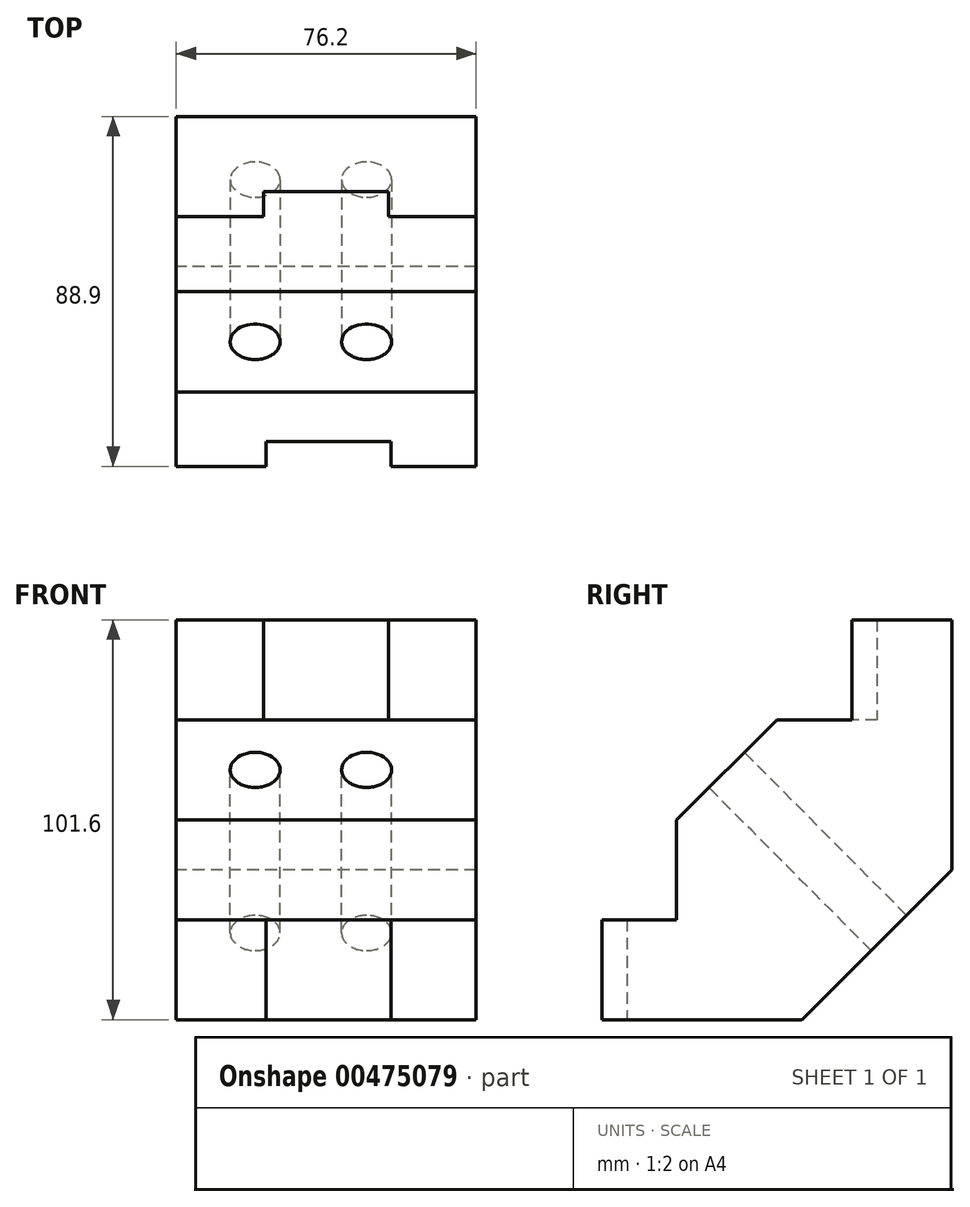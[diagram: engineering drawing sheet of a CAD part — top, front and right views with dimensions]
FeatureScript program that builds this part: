
annotation { "Feature Type Name" : "Feature", "Feature Type Description" : "" }
export const myFeature = defineFeature(function(context is Context, id is Id, definition is map)
    precondition{}
    {
        {
            var Q0;
            Q0=qCreatedBy(makeId("Right.planeOp"),FACE);
            var sketch = newSketch(context, id + "F0", { "sketchPlane" : qUnion([Q0])});
            skLineSegment(sketch, "E0", {"start": v(0, 0) * mm, "end": v(50.8, 0) * mm});
            skLineSegment(sketch, "E1", {"start": v(50.8, 0) * mm, "end": v(88.9, 38.1) * mm});
            skLineSegment(sketch, "E2", {"start": v(88.9, 38.1) * mm, "end": v(88.9, 101.6) * mm});
            skLineSegment(sketch, "E3", {"start": v(88.9, 101.6) * mm, "end": v(63.5, 101.6) * mm});
            skLineSegment(sketch, "E4", {"start": v(63.5, 101.6) * mm, "end": v(63.5, 76.2) * mm});
            skLineSegment(sketch, "E5", {"start": v(63.5, 76.2) * mm, "end": v(44.45, 76.2) * mm});
            skLineSegment(sketch, "E6", {"start": v(44.45, 76.2) * mm, "end": v(18.9, 50.8) * mm});
            skLineSegment(sketch, "E7", {"start": v(18.9, 50.8) * mm, "end": v(18.9, 25.4) * mm});
            skLineSegment(sketch, "E8", {"start": v(18.9, 25.4) * mm, "end": v(0, 25.4) * mm});
            skLineSegment(sketch, "E9", {"start": v(0, 25.4) * mm, "end": v(0, 0) * mm});
            skSolve(sketch);
        }
        {
            var Q0;
            Q0 = qSketchRegion(id + "F0", true);
            extrude(context, id + "F1", {"entities" : qUnion([Q0]), "depth" : 76.2 * mm});
        }
        {
            var Q0;
            Q0=makeQuery(id+"F1.opExtrude","SWEPT_FACE",FACE,{"disambiguationData":[OSD([sQuery(id+"F0.wireOp",EDGE,"E4")])]});
            var sketch = newSketch(context, id + "F2", { "sketchPlane" : qUnion([Q0])});
            skLineSegment(sketch, "E10", {"start": v(22.23, 101.6) * mm, "end": v(22.23, 76.2) * mm});
            skLineSegment(sketch, "E11", {"start": v(22.23, 76.2) * mm, "end": v(53.98, 76.2) * mm});
            skLineSegment(sketch, "E12", {"start": v(53.98, 76.2) * mm, "end": v(53.98, 101.6) * mm});
            skLineSegment(sketch, "E13", {"start": v(53.98, 101.6) * mm, "end": v(22.23, 101.6) * mm});
            skSolve(sketch);
        }
        {
            var Q0;
            Q0 = qSketchRegion(id + "F2", true);
            extrude(context, id + "F3", {"entities" : qUnion([Q0]), "operationType" : NewBodyOperationType.REMOVE, "oppositeDirection" : true, "depth" : 6.35 * mm});
        }
        {
            var Q0;
            Q0=makeQuery(id+"F1.opExtrude","SWEPT_FACE",FACE,{"disambiguationData":[OSD([sQuery(id+"F0.wireOp",EDGE,"E9")])]});
            var sketch = newSketch(context, id + "F4", { "sketchPlane" : qUnion([Q0])});
            skLineSegment(sketch, "E14", {"start": v(22.86, 25.4) * mm, "end": v(54.6, 25.4) * mm});
            skLineSegment(sketch, "E15", {"start": v(54.6, 25.4) * mm, "end": v(54.6, 0) * mm});
            skLineSegment(sketch, "E16", {"start": v(54.6, 0) * mm, "end": v(22.86, 0) * mm});
            skLineSegment(sketch, "E17", {"start": v(22.86, 0) * mm, "end": v(22.86, 25.4) * mm});
            skSolve(sketch);
        }
        {
            var Q0;
            Q0=makeQuery(id+"F4.imprint","IMPRINT",FACE,{"disambiguationData":[TD([[makeQuery(id+"F4.imprint","IMPRINT",EDGE,{"derivedFrom":sQuery(id+"F4.wireOp",EDGE,"E14")}),1.0]])]});
            extrude(context, id + "F5", {"entities" : qUnion([Q0]), "operationType" : NewBodyOperationType.REMOVE, "oppositeDirection" : true, "depth" : 6.35 * mm});
        }
        {
            var Q0;
            Q0=makeQuery(id+"F1.opExtrude","SWEPT_FACE",FACE,{"disambiguationData":[OSD([sQuery(id+"F0.wireOp",EDGE,"E6")])]});
            var sketch = newSketch(context, id + "F6", { "sketchPlane" : qUnion([Q0])});
            skCircle(sketch, "E18", {"center": v(20.08, 67.18) * mm, "radius": 6.35 * mm});
            skCircle(sketch, "E19", {"center": v(48.38, 67.18) * mm, "radius": 6.35 * mm});
            skSolve(sketch);
        }
        {
            var Q0;
            Q0 = qSketchRegion(id + "F6", true);
            extrude(context, id + "F7", {"entities" : qUnion([Q0]), "operationType" : NewBodyOperationType.REMOVE, "oppositeDirection" : true, "depth" : 80.52 * mm});
        }
    });
